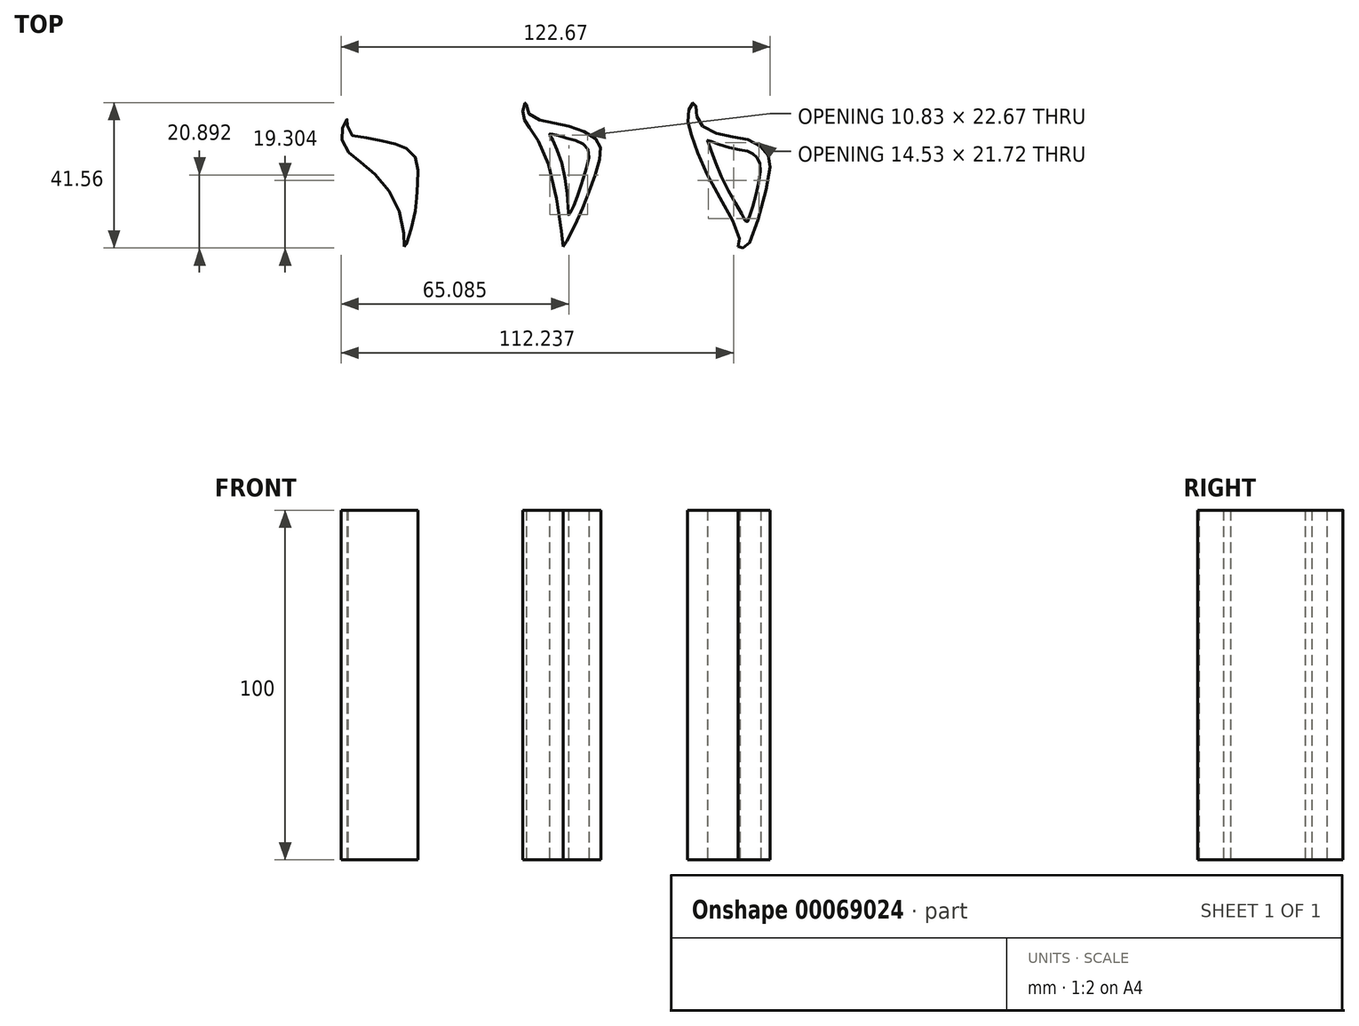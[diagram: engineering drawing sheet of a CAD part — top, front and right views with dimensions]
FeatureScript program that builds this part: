
annotation { "Feature Type Name" : "Feature", "Feature Type Description" : "" }
export const myFeature = defineFeature(function(context is Context, id is Id, definition is map)
    precondition{}
    {
        {
            var Q0;
            Q0=qCreatedBy(makeId("Top.planeOp"),FACE);
            var sketch = newSketch(context, id + "F0", { "sketchPlane" : qUnion([Q0])});
            skPoint(sketch, "E0", {"position": v(0, 0) * mm});
            skPoint(sketch, "E1", {"position": v(0, 35) * mm});
            skFitSpline(sketch, "E2", {"points": [v(0, 0) * mm, v(-4.14, 23.28) * mm, v(-9.97, 34.47) * mm, v(-11.15, 36.41) * mm, v(-11.57, 38.76) * mm, v(-10.88, 41.04) * mm, v(-10.84, 41.12) * mm, v(-10.66, 41.16) * mm, v(-10.56, 41) * mm, v(-10.6, 40.66) * mm, v(-9.64, 37.75) * mm, v(-4.55, 35.74) * mm, v(2.4, 34.17) * mm, v(8.7, 31.3) * mm, v(10.64, 28.65) * mm, v(10.2, 24.07) * mm, v(7.33, 15.38) * mm, v(3.55, 6.45) * mm, v(0.11, 0.02) * mm, v(0.02, -0.04) * mm, v(0, -0.02) * mm, v(0, 0) * mm]});
            skFitSpline(sketch, "E3", {"points": [v(-3.82, 31.83) * mm, v(0, 22.24) * mm, v(1.47, 9.4) * mm, v(1.47, 9.3) * mm, v(1.56, 8.97) * mm, v(3.13, 11.9) * mm, v(6.1, 20.62) * mm, v(6.95, 28.17) * mm, v(1.6, 30.87) * mm, v(-3.2, 32.2) * mm, v(-3.8, 32.22) * mm, v(-3.97, 32.05) * mm, v(-3.82, 31.83) * mm]});
            skLineSegment(sketch, "E4", {"start": v(-10.66, 41.16) * mm, "end": v(82.12, 41) * mm, "construction": true});
            skPoint(sketch, "E5.4.internal.snap0", {"position": v(35.73, 41.08) * mm});
            skFitSpline(sketch, "E5", {"points": [v(50.05, 0) * mm, v(50.47, 2.22) * mm, v(41.78, 19.4) * mm, v(36.41, 32.96) * mm, v(35.73, 38.23) * mm, v(37.07, 41.08) * mm, v(37.15, 41.08) * mm, v(37.5, 41.08) * mm, v(38.08, 39.17) * mm, v(38.88, 35.48) * mm, v(45.76, 31.9) * mm, v(53.84, 30.2) * mm, v(58.33, 26.6) * mm, v(58.92, 20.92) * mm, v(52.64, 0) * mm, v(51.19, -0.3) * mm, v(50.05, -0.07) * mm, v(50.05, 0) * mm]});
            skFitSpline(sketch, "E6", {"points": [v(41.48, 29.77) * mm, v(45.06, 20.43) * mm, v(51.4, 8.7) * mm, v(52.53, 7) * mm, v(53.12, 8) * mm, v(55.18, 15.07) * mm, v(56.37, 23.5) * mm, v(55.03, 25.94) * mm, v(53.23, 27.09) * mm, v(48.25, 28.13) * mm, v(42.06, 30.13) * mm, v(41.36, 30.38) * mm, v(41.22, 30.33) * mm, v(41.48, 29.77) * mm]});
            skFitSpline(sketch, "E7", {"points": [v(-45.47, 0) * mm, v(-46.54, 9.13) * mm, v(-54.77, 21.59) * mm, v(-61.31, 26.95) * mm, v(-63.5, 32.07) * mm, v(-62.32, 35.67) * mm, v(-61.57, 36.51) * mm, v(-61.65, 32.9) * mm, v(-57.29, 31.23) * mm, v(-50.08, 29.8) * mm, v(-45.55, 28.46) * mm, v(-42.28, 25.44) * mm, v(-41.52, 19.9) * mm, v(-41.86, 14.2) * mm, v(-42.78, 7.83) * mm, v(-45.07, 0.17) * mm, v(-45.42, -0.26) * mm, v(-45.47, 0) * mm]});
            skSolve(sketch);
        }
        {
            var Q0;
            Q0=makeQuery(id+"F0.imprint","IMPRINT",FACE,{"disambiguationData":[TD([[makeQuery(id+"F0.imprint","IMPRINT",EDGE,{"derivedFrom":sQuery(id+"F0.wireOp",EDGE,"E2")}),-1.0]])]});
            var Q1;
            Q1=makeQuery(id+"F0.imprint","IMPRINT",FACE,{"disambiguationData":[TD([[makeQuery(id+"F0.imprint","IMPRINT",EDGE,{"derivedFrom":sQuery(id+"F0.wireOp",EDGE,"E5")}),-1.0]])]});
            var Q2;
            Q2=makeQuery(id+"F0.imprint","IMPRINT",FACE,{"disambiguationData":[TD([[makeQuery(id+"F0.imprint","IMPRINT",EDGE,{"derivedFrom":sQuery(id+"F0.wireOp",EDGE,"E7")}),-1.0]])]});
            extrude(context, id + "F1", {"entities" : qUnion([Q0, Q1, Q2]), "depth" : 100 * mm});
        }
    });
